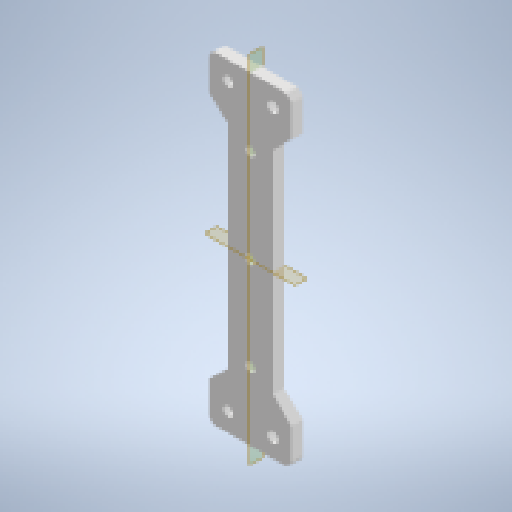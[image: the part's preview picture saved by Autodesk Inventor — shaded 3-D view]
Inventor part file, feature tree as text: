
AUTODESK INVENTOR PART (.ipt)
format: ipt  version: 2023 (Build 270158000, 158)  size: 239,616 bytes
history: native  units: in
note: dims shown in document units (in); Inventor stores cm internally (conversion verified against a paired STEP export)
features: extrude x4, sketch x4, other x4, plane x2, reference x2, projected_geometry x2, mirror x1, pattern_linear x1, fillet x1
ambient origin geometry x8: Origin, YZ Plane, XZ Plane, XY Plane, X Axis, Y Axis, Z Axis, Center Point
bodies: Solid1 (feature_tree)
feature tree (21):
  extrude  "Extrusion1"  Depth=0.1083in
  extrude  "Extrusion2"  Depth=0.1083in
  plane  "Work Plane1"
  mirror  "Mirror1"
  extrude  "Extrusion3"  Depth=0.1181in TaperAngle=0.0deg
  extrude  "Extrusion4"  TaperAngle=45.0deg  [1 undecoded]
  pattern_linear  "Rectangular Pattern1"  Spacing1=45.0deg  [1 undecoded]
  plane  "Work Plane2"
  fillet  "Fillet1"  Radius=0.3937in
  sketch  "Sketch1"  dims[d0=0.1083in d1=0.1083in]
  reference  "Reference1"
  reference  "Reference2"
  sketch  "Sketch2"  dims[d2=0.1083in d3=0.1083in]
  projected_geometry  "Projected Loop1"
  sketch  "Sketch3"  dims[d4=0.1969in d5=0.1181in d6=0.0in]
  projected_geometry  "Projected Loop2"
  sketch  "Sketch4"  dims[d7=0.1969in d8=45.0deg d9=45.0deg d10=0.3937in d11=0.3937in d12=0.0in d13=0.0in d14=0.0984in d15=1.7047in d16=3.4094in d17=0.0in d18=0.0in d19=0.1772in d20=0.0787in d21=0.0in d22=1.1811in d24=0.9843in d25=0.0787in]
  parser-record x1  (decoder bookkeeping rows leaked as tree rows — omitted from the tree; the rows remain in map.json)
  other  "A.iam"
  other  "A-04:1"
  other  "A-04:2"
note: 2 required parameter values undecoded (feature->parameter linkage not recoverable at this tier; creation-order binding heuristic only, values carry confidence <= 0.55)
note: 1 file-system path scrubbed to <path> (originals preserved in map.json)
